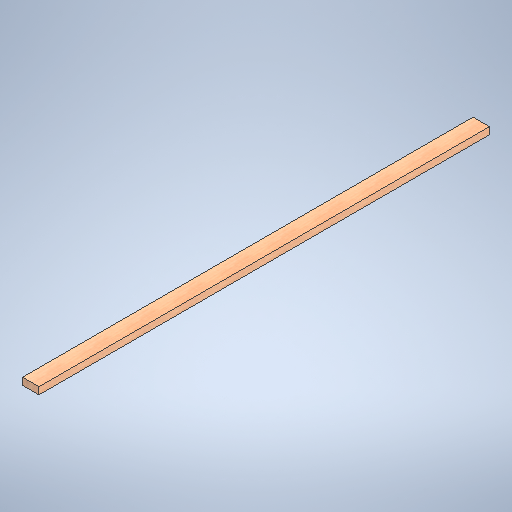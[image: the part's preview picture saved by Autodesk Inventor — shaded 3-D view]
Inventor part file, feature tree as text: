
AUTODESK INVENTOR PART (.ipt)
format: ipt  version: 2025.1 (Build 291241020, 241B)  size: 283,648 bytes
history: native  units: in
note: dims shown in document units (in); Inventor stores cm internally (conversion verified against a paired STEP export)
features: extrude x1, sketch x1
ambient origin geometry x8: Origin, YZ Plane, XZ Plane, XY Plane, X Axis, Y Axis, Z Axis, Center Point
bodies: Solid1 (feature_tree)
feature tree (2):
  extrude  "Extrusion1"  Depth=1.5in
  sketch  "Sketch1"  dims[d0=3.5in d1=1.5in d2=96.0in d3=0.0in]
